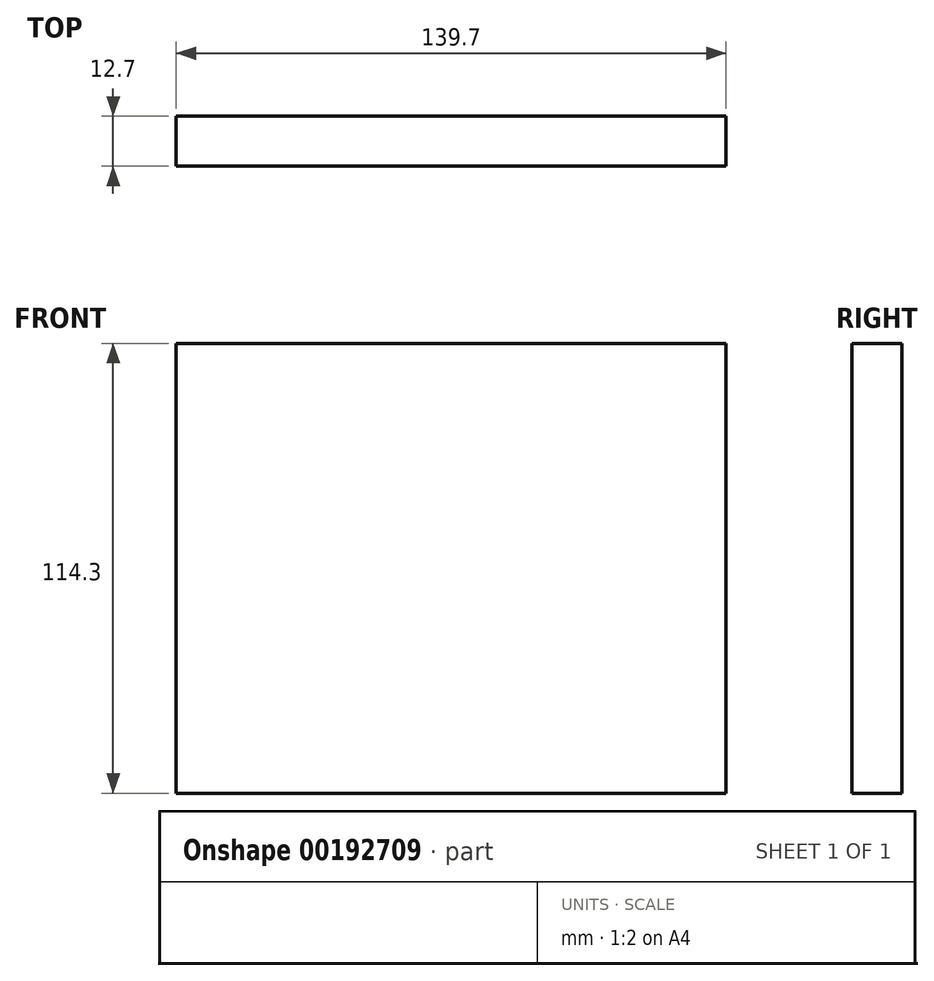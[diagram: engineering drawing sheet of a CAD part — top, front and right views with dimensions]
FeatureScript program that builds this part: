
annotation { "Feature Type Name" : "Feature", "Feature Type Description" : "" }
export const myFeature = defineFeature(function(context is Context, id is Id, definition is map)
    precondition{}
    {
        {
            var Q0;
            Q0=qCreatedBy(makeId("Front.planeOp"),FACE);
            var sketch = newSketch(context, id + "F0", { "sketchPlane" : qUnion([Q0])});
            skLineSegment(sketch, "E0.bottom", {"start": v(-92.77, -37.86) * mm, "end": v(110.43, -37.86) * mm});
            skLineSegment(sketch, "E0.top", {"start": v(-92.77, 165.34) * mm, "end": v(110.43, 165.34) * mm});
            skLineSegment(sketch, "E0.left", {"start": v(-92.77, -37.86) * mm, "end": v(-92.77, 165.34) * mm});
            skLineSegment(sketch, "E0.right", {"start": v(110.43, -37.86) * mm, "end": v(110.43, 165.34) * mm});
            skLineSegment(sketch, "E1.0", {"start": v(-92.77, 114.54) * mm, "end": v(110.43, 114.54) * mm});
            skLineSegment(sketch, "E2.0", {"start": v(-92.77, 12.94) * mm, "end": v(110.43, 12.94) * mm});
            skLineSegment(sketch, "E3.0", {"start": v(-92.77, 25.64) * mm, "end": v(110.43, 25.64) * mm});
            skLineSegment(sketch, "E4.0", {"start": v(-92.77, 101.84) * mm, "end": v(110.43, 101.84) * mm});
            skLineSegment(sketch, "E5", {"start": v(8.83, 165.34) * mm, "end": v(8.83, -37.86) * mm});
            skLineSegment(sketch, "E6.bottom", {"start": v(110.43, 114.54) * mm, "end": v(8.83, 114.54) * mm});
            skLineSegment(sketch, "E6.top", {"start": v(110.43, 101.84) * mm, "end": v(8.83, 101.84) * mm});
            skLineSegment(sketch, "E6.left", {"start": v(110.43, 114.54) * mm, "end": v(110.43, 101.84) * mm});
            skLineSegment(sketch, "E6.right", {"start": v(8.83, 114.54) * mm, "end": v(8.83, 101.84) * mm});
            skLineSegment(sketch, "E7.bottom", {"start": v(110.43, 25.64) * mm, "end": v(8.83, 25.64) * mm});
            skLineSegment(sketch, "E7.top", {"start": v(110.43, 12.94) * mm, "end": v(8.83, 12.94) * mm});
            skLineSegment(sketch, "E7.left", {"start": v(110.43, 25.64) * mm, "end": v(110.43, 12.94) * mm});
            skLineSegment(sketch, "E7.right", {"start": v(8.83, 25.64) * mm, "end": v(8.83, 12.94) * mm});
            skSolve(sketch);
        }
        {
            var Q0;
            {var subQ5=sQuery(id+"F0.wireOp",EDGE,"E2.0");Q0=makeQuery(id+"F0.imprint","IMPRINT",FACE,{"disambiguationData":[TD([[makeQuery(id+"F0.imprint","IMPRINT",EDGE,{"derivedFrom":subQ5}),-1.0]])]});}
            var Q1;
            {var subQ5=sQuery(id+"F0.wireOp",EDGE,"E7.top");Q1=makeQuery(id+"F0.imprint","IMPRINT",FACE,{"disambiguationData":[TD([[makeQuery(id+"F0.imprint","IMPRINT",EDGE,{"derivedFrom":subQ5}),1.0]])]});}
            var Q2;
            {var subQ5=sQuery(id+"F0.wireOp",EDGE,"E1.0");Q2=makeQuery(id+"F0.imprint","IMPRINT",FACE,{"disambiguationData":[TD([[makeQuery(id+"F0.imprint","IMPRINT",EDGE,{"derivedFrom":subQ5}),1.0]])]});}
            var Q3;
            {var subQ5=sQuery(id+"F0.wireOp",EDGE,"E6.bottom");Q3=makeQuery(id+"F0.imprint","IMPRINT",FACE,{"disambiguationData":[TD([[makeQuery(id+"F0.imprint","IMPRINT",EDGE,{"derivedFrom":subQ5}),-1.0]])]});}
            var Q4;
            {var subQ0=sQuery(id+"F0.wireOp",EDGE,"E2.0");Q4=makeQuery(id+"F0.imprint","IMPRINT",FACE,{"disambiguationData":[TD([[makeQuery(id+"F0.imprint","IMPRINT",EDGE,{"derivedFrom":subQ0}),1.0]])]});}
            var Q5;
            {var subQ0=sQuery(id+"F0.wireOp",EDGE,"E3.0");Q5=makeQuery(id+"F0.imprint","IMPRINT",FACE,{"disambiguationData":[TD([[makeQuery(id+"F0.imprint","IMPRINT",EDGE,{"derivedFrom":subQ0}),1.0]])]});}
            var Q6;
            {var subQ0=sQuery(id+"F0.wireOp",EDGE,"E1.0");Q6=makeQuery(id+"F0.imprint","IMPRINT",FACE,{"disambiguationData":[TD([[makeQuery(id+"F0.imprint","IMPRINT",EDGE,{"derivedFrom":subQ0}),-1.0]])]});}
            var Q7;
            {var subQ0=sQuery(id+"F0.wireOp",EDGE,"E6.top");Q7=makeQuery(id+"F0.imprint","IMPRINT",FACE,{"disambiguationData":[TD([[makeQuery(id+"F0.imprint","IMPRINT",EDGE,{"derivedFrom":subQ0}),1.0]])]});}
            extrude(context, id + "F1", {"entities" : qUnion([Q0, Q1, Q2, Q3, Q4, Q5, Q6, Q7]), "oppositeDirection" : true, "depth" : 12.7 * mm});
        }
        {
            var Q0;
            Q0=makeQuery(id+"F1.opExtrude","CAP_FACE",FACE,{"disambiguationData":[OSD([sQuery(id+"F0.wireOp",EDGE,"E0.bottom"),sQuery(id+"F0.wireOp",EDGE,"E0.top"),sQuery(id+"F0.wireOp",EDGE,"E0.left"),sQuery(id+"F0.wireOp",EDGE,"E0.right"),sQuery(id+"F0.wireOp",EDGE,"E6.bottom"),sQuery(id+"F0.wireOp",EDGE,"E6.top"),sQuery(id+"F0.wireOp",EDGE,"E6.right"),sQuery(id+"F0.wireOp",EDGE,"E7.bottom"),sQuery(id+"F0.wireOp",EDGE,"E7.top"),sQuery(id+"F0.wireOp",EDGE,"E7.right")])],"isStart":true});
            var sketch = newSketch(context, id + "F2", { "sketchPlane" : qUnion([Q0])});
            skPoint(sketch, "E8.oppositeSnap0", {"position": v(59.63, 12.94) * mm});
            skLineSegment(sketch, "E8.bottom", {"start": v(110.43, 165.34) * mm, "end": v(59.63, 165.34) * mm});
            skLineSegment(sketch, "E8.top", {"start": v(110.43, -37.86) * mm, "end": v(59.63, -37.86) * mm});
            skLineSegment(sketch, "E8.left", {"start": v(110.43, 165.34) * mm, "end": v(110.43, -37.86) * mm});
            skLineSegment(sketch, "E8.right", {"start": v(59.63, 165.34) * mm, "end": v(59.63, -37.86) * mm});
            skSolve(sketch);
        }
        {
            var Q0;
            Q0 = qSketchRegion(id + "F2", true);
            extrude(context, id + "F3", {"entities" : qUnion([Q0]), "operationType" : NewBodyOperationType.REMOVE, "oppositeDirection" : true, "depth" : 25.4 * mm});
        }
        {
            var Q0;
            Q0=makeQuery(id+"F1.opExtrude","CAP_FACE",FACE,{"disambiguationData":[OSD([sQuery(id+"F0.wireOp",EDGE,"E0.bottom"),sQuery(id+"F0.wireOp",EDGE,"E0.top"),sQuery(id+"F0.wireOp",EDGE,"E0.left"),sQuery(id+"F0.wireOp",EDGE,"E0.right"),sQuery(id+"F0.wireOp",EDGE,"E6.bottom"),sQuery(id+"F0.wireOp",EDGE,"E6.top"),sQuery(id+"F0.wireOp",EDGE,"E6.right"),sQuery(id+"F0.wireOp",EDGE,"E7.bottom"),sQuery(id+"F0.wireOp",EDGE,"E7.top"),sQuery(id+"F0.wireOp",EDGE,"E7.right")])],"isStart":true});
            var sketch = newSketch(context, id + "F4", { "sketchPlane" : qUnion([Q0])});
            skLineSegment(sketch, "E9.0", {"start": v(46.93, 165.34) * mm, "end": v(46.93, 114.54) * mm});
            skLineSegment(sketch, "E10", {"start": v(46.93, 165.34) * mm, "end": v(46.93, -37.86) * mm});
            skLineSegment(sketch, "E11.bottom", {"start": v(46.93, 165.34) * mm, "end": v(59.63, 165.34) * mm});
            skLineSegment(sketch, "E11.top", {"start": v(46.93, -37.86) * mm, "end": v(59.63, -37.86) * mm});
            skLineSegment(sketch, "E11.right", {"start": v(59.63, 165.34) * mm, "end": v(59.63, -37.86) * mm});
            skSolve(sketch);
        }
        {
            var Q0;
            {var subQ0=sQuery(id+"F4.wireOp",EDGE,"E11.bottom");Q0=makeQuery(id+"F4.imprint","IMPRINT",FACE,{"disambiguationData":[TD([[makeQuery(id+"F4.imprint","IMPRINT",EDGE,{"derivedFrom":subQ0}),-1.0]])]});}
            var Q1;
            {var subQ0=sQuery(id+"F4.wireOp",EDGE,"E11.top");Q1=makeQuery(id+"F4.imprint","IMPRINT",FACE,{"disambiguationData":[TD([[makeQuery(id+"F4.imprint","IMPRINT",EDGE,{"derivedFrom":subQ0}),1.0]])]});}
            var Q2;
            {var subQ0=sQuery(id+"F4.wireOp",EDGE,"E10");var subQ1=makeQuery(id+"F1.opExtrude","CAP_EDGE",EDGE,{"disambiguationData":[OSD([sQuery(id+"F0.wireOp",EDGE,"E6.top")])],"isStart":true});var subQ2=makeQuery(id+"F4.imprint","INTERSECT",VERTEX,{"derivedFrom":[subQ1,subQ0]});Q2=makeQuery(id+"F4.imprint","IMPRINT",FACE,{"disambiguationData":[TD([[makeQuery(id+"F4.imprint","IMPRINT",EDGE,{"disambiguationData":[TD([[subQ2,-1.0]])],"derivedFrom":subQ0}),1.0]])]});}
            extrude(context, id + "F5", {"entities" : qUnion([Q0, Q1, Q2]), "operationType" : NewBodyOperationType.REMOVE, "oppositeDirection" : true, "depth" : 25.4 * mm});
        }
        {
            var Q0;
            Q0=makeQuery(id+"F1.opExtrude","CAP_FACE",FACE,{"disambiguationData":[OSD([sQuery(id+"F0.wireOp",EDGE,"E0.bottom"),sQuery(id+"F0.wireOp",EDGE,"E0.top"),sQuery(id+"F0.wireOp",EDGE,"E0.left"),sQuery(id+"F0.wireOp",EDGE,"E0.right"),sQuery(id+"F0.wireOp",EDGE,"E6.bottom"),sQuery(id+"F0.wireOp",EDGE,"E6.top"),sQuery(id+"F0.wireOp",EDGE,"E6.right"),sQuery(id+"F0.wireOp",EDGE,"E7.bottom"),sQuery(id+"F0.wireOp",EDGE,"E7.top"),sQuery(id+"F0.wireOp",EDGE,"E7.right")])],"isStart":true});
            var sketch = newSketch(context, id + "F6", { "sketchPlane" : qUnion([Q0])});
            skLineSegment(sketch, "E12.0", {"start": v(-92.77, 120.89) * mm, "end": v(46.93, 120.89) * mm});
            skLineSegment(sketch, "E13.0", {"start": v(-92.77, 6.59) * mm, "end": v(46.93, 6.59) * mm});
            skSolve(sketch);
        }
        {
            var Q0;
            Q0 = qSketchRegion(id + "F6", true);
            var Q1;
            {var subQ0=sQuery(id+"F6.wireOp",EDGE,"E12.0");Q1=makeQuery(id+"F6.imprint","IMPRINT",FACE,{"disambiguationData":[TD([[makeQuery(id+"F6.imprint","IMPRINT",EDGE,{"derivedFrom":subQ0}),1.0]])]});}
            var Q2;
            {var subQ0=sQuery(id+"F6.wireOp",EDGE,"E13.0");Q2=makeQuery(id+"F6.imprint","IMPRINT",FACE,{"disambiguationData":[TD([[makeQuery(id+"F6.imprint","IMPRINT",EDGE,{"derivedFrom":subQ0}),-1.0]])]});}
            extrude(context, id + "F7", {"entities" : qUnion([Q0, Q1, Q2]), "operationType" : NewBodyOperationType.REMOVE, "oppositeDirection" : true, "depth" : 25.4 * mm});
        }
    });
